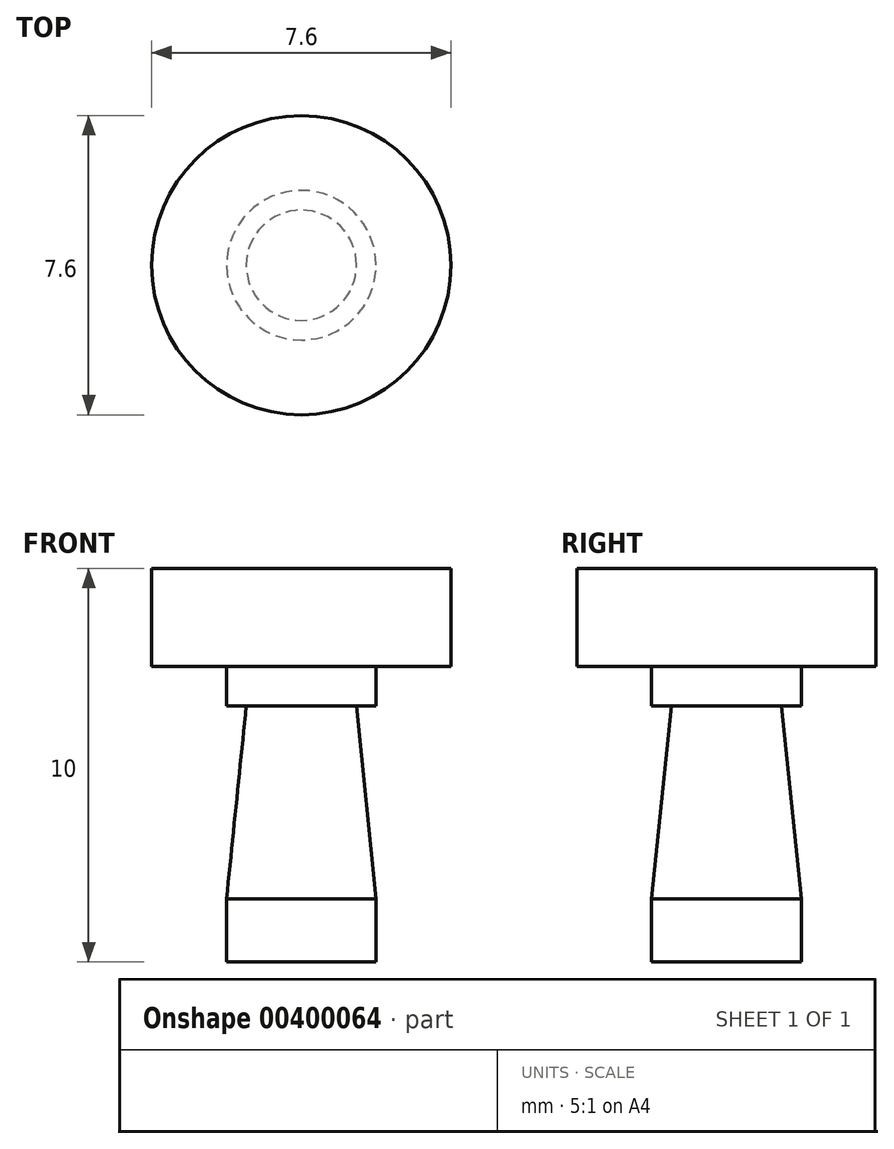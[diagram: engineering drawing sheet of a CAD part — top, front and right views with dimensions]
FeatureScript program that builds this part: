
annotation { "Feature Type Name" : "Feature", "Feature Type Description" : "" }
export const myFeature = defineFeature(function(context is Context, id is Id, definition is map)
    precondition{}
    {
        {
            var Q0;
            Q0=qCreatedBy(makeId("Front.planeOp"),FACE);
            var sketch = newSketch(context, id + "F0", { "sketchPlane" : qUnion([Q0])});
            skLineSegment(sketch, "E0", {"start": v(0, 0) * mm, "end": v(3.8, 0) * mm});
            skLineSegment(sketch, "E1", {"start": v(3.8, 0) * mm, "end": v(3.8, -2.5) * mm});
            skLineSegment(sketch, "E2", {"start": v(3.8, -2.5) * mm, "end": v(1.9, -2.5) * mm});
            skLineSegment(sketch, "E3", {"start": v(1.9, -2.5) * mm, "end": v(1.9, -3.5) * mm});
            skLineSegment(sketch, "E4", {"start": v(1.9, -10) * mm, "end": v(0, -10) * mm});
            skLineSegment(sketch, "E5", {"start": v(0, -10) * mm, "end": v(0, 0) * mm});
            skLineSegment(sketch, "E6", {"start": v(1.9, -3.5) * mm, "end": v(1.4, -3.5) * mm});
            skLineSegment(sketch, "E7", {"start": v(1.4, -3.5) * mm, "end": v(1.9, -8.4) * mm});
            skLineSegment(sketch, "E8.trimOffspring", {"start": v(1.9, -8.4) * mm, "end": v(1.9, -10) * mm});
            skSolve(sketch);
        }
        {
            var Q0;
            Q0 = qSketchRegion(id + "F0", true);
            var Q1;
            Q1=sQuery(id+"F0.wireOp",EDGE,"E5");
            revolve(context, id + "F1", {"entities" : qUnion([Q0]), "axis" : qUnion([Q1]), "revolveType" : RevolveType.FULL});
        }
    });
